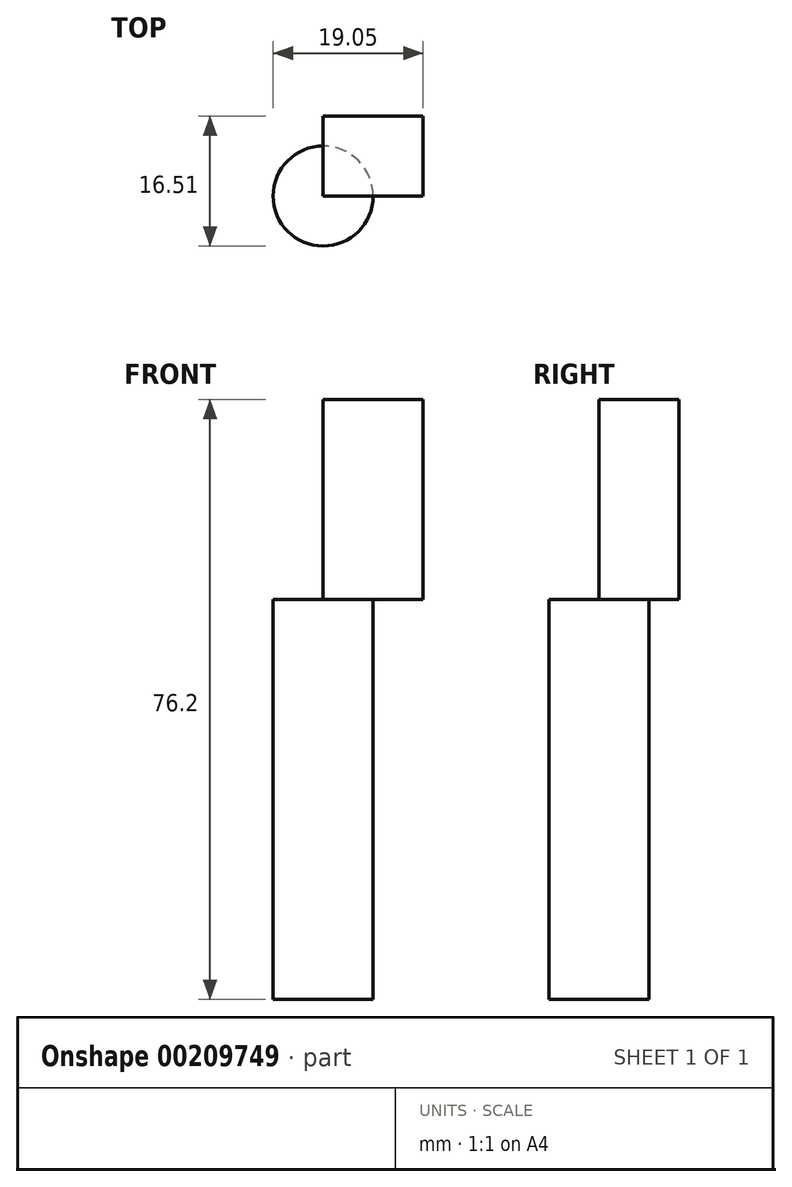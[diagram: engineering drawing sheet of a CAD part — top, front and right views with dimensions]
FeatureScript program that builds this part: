
annotation { "Feature Type Name" : "Feature", "Feature Type Description" : "" }
export const myFeature = defineFeature(function(context is Context, id is Id, definition is map)
    precondition{}
    {
        {
            var Q0;
            Q0=qCreatedBy(makeId("Front.planeOp"),FACE);
            var sketch = newSketch(context, id + "F0", { "sketchPlane" : qUnion([Q0])});
            skLineSegment(sketch, "E0.bottom", {"start": v(0, 0) * mm, "end": v(6.35, 0) * mm});
            skLineSegment(sketch, "E0.top", {"start": v(0, 50.8) * mm, "end": v(6.35, 50.8) * mm});
            skLineSegment(sketch, "E0.left", {"start": v(0, 0) * mm, "end": v(0, 50.8) * mm});
            skLineSegment(sketch, "E0.right", {"start": v(6.35, 0) * mm, "end": v(6.35, 50.8) * mm});
            skSolve(sketch);
        }
        {
            var Q0;
            Q0 = qSketchRegion(id + "F0", true);
            var Q1;
            Q1=sQuery(id+"F0.wireOp",EDGE,"E0.left");
            revolve(context, id + "F1", {"entities" : qUnion([Q0]), "axis" : qUnion([Q1]), "revolveType" : RevolveType.FULL});
        }
        {
            var Q0;
            Q0=makeQuery(id+"F1.opRevolve","SWEPT_FACE",FACE,{"disambiguationData":[OSD([sQuery(id+"F0.wireOp",EDGE,"E0.top")])]});
            var sketch = newSketch(context, id + "F2", { "sketchPlane" : qUnion([Q0])});
            skLineSegment(sketch, "E1.bottom", {"start": v(0, 0) * mm, "end": v(12.7, 0) * mm});
            skLineSegment(sketch, "E1.top", {"start": v(0, 10.16) * mm, "end": v(12.7, 10.16) * mm});
            skLineSegment(sketch, "E1.left", {"start": v(0, 0) * mm, "end": v(0, 10.16) * mm});
            skLineSegment(sketch, "E1.right", {"start": v(12.7, 0) * mm, "end": v(12.7, 10.16) * mm});
            skSolve(sketch);
        }
        {
            var Q0;
            Q0 = qSketchRegion(id + "F2", true);
            extrude(context, id + "F3", {"entities" : qUnion([Q0]), "operationType" : NewBodyOperationType.ADD, "depth" : 25.4 * mm});
        }
    });
